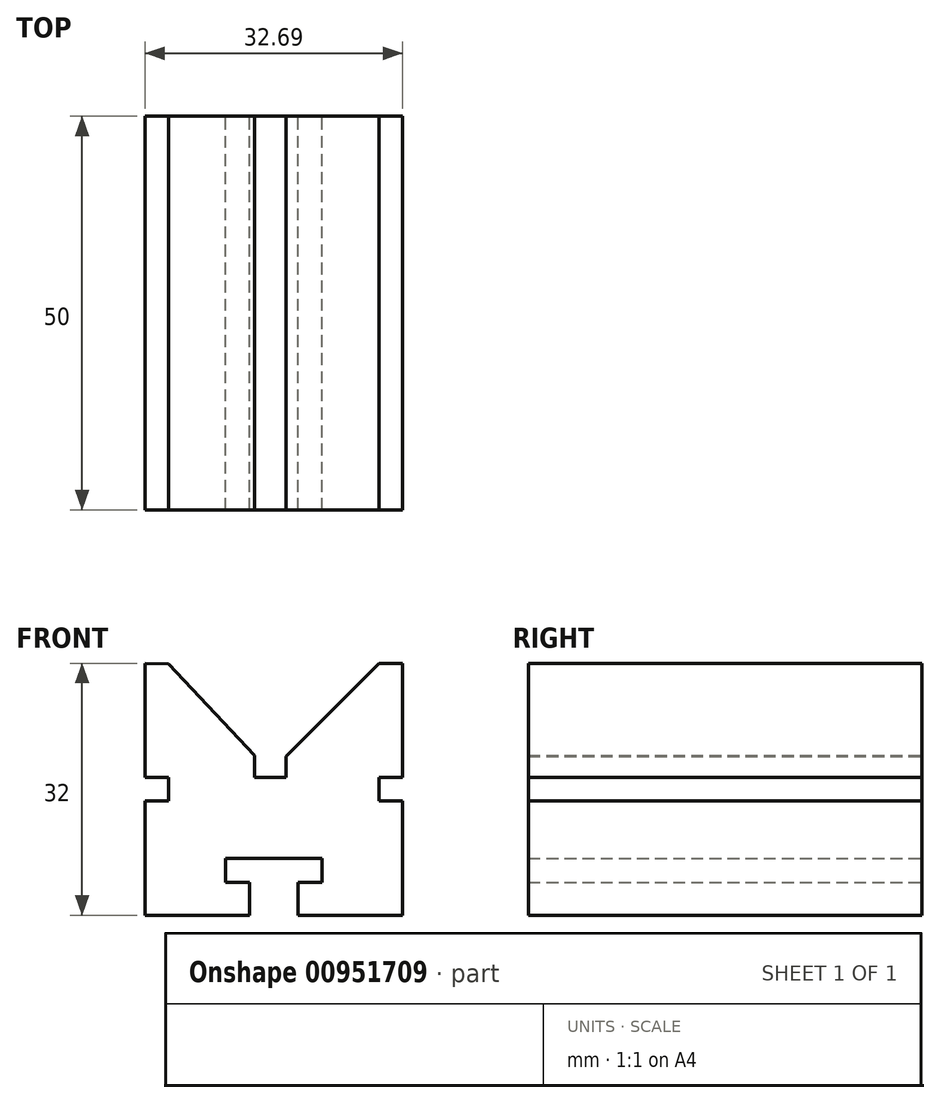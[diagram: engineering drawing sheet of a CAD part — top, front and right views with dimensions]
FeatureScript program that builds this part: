
annotation { "Feature Type Name" : "Feature", "Feature Type Description" : "" }
export const myFeature = defineFeature(function(context is Context, id is Id, definition is map)
    precondition{}
    {
        {
            var Q0;
            Q0=qCreatedBy(makeId("Front.planeOp"),FACE);
            var sketch = newSketch(context, id + "F0", { "sketchPlane" : qUnion([Q0])});
            skLineSegment(sketch, "E0.bottom", {"start": v(0, 0) * mm, "end": v(-13.24, 0) * mm});
            skLineSegment(sketch, "E0.left", {"start": v(0, 0) * mm, "end": v(0, 14.5) * mm});
            skLineSegment(sketch, "E0.right", {"start": v(-32.69, 0) * mm, "end": v(-32.69, 14.5) * mm});
            skLineSegment(sketch, "E1", {"start": v(-32.69, 32) * mm, "end": v(-29.69, 31.9) * mm});
            skLineSegment(sketch, "E2", {"start": v(-29.69, 31.9) * mm, "end": v(-18.8, 20.32) * mm});
            skPoint(sketch, "E2.endSnap0", {"position": v(-16.8, 32.44) * mm});
            skLineSegment(sketch, "E3", {"start": v(-14.8, 20.2) * mm, "end": v(-3, 32) * mm});
            skLineSegment(sketch, "E4", {"start": v(-3, 32) * mm, "end": v(0, 32) * mm});
            skLineSegment(sketch, "E5", {"start": v(0, 32) * mm, "end": v(0, 17.5) * mm});
            skLineSegment(sketch, "E6", {"start": v(0, 17.5) * mm, "end": v(-3, 17.5) * mm});
            skLineSegment(sketch, "E7", {"start": v(-3, 17.5) * mm, "end": v(-3, 14.5) * mm});
            skLineSegment(sketch, "E8", {"start": v(-3, 14.5) * mm, "end": v(0, 14.5) * mm});
            skLineSegment(sketch, "E9", {"start": v(-32.69, 17.5) * mm, "end": v(-29.69, 17.5) * mm});
            skLineSegment(sketch, "E10", {"start": v(-29.69, 17.5) * mm, "end": v(-29.69, 14.5) * mm});
            skLineSegment(sketch, "E11", {"start": v(-29.69, 14.5) * mm, "end": v(-32.69, 14.5) * mm});
            skLineSegment(sketch, "E12", {"start": v(-32.69, 0) * mm, "end": v(-19.44, 0) * mm});
            skLineSegment(sketch, "E13", {"start": v(-19.44, 0) * mm, "end": v(-19.44, 4.2) * mm});
            skLineSegment(sketch, "E14", {"start": v(-19.44, 4.2) * mm, "end": v(-22.44, 4.2) * mm});
            skLineSegment(sketch, "E15", {"start": v(-22.44, 4.2) * mm, "end": v(-22.44, 7.2) * mm});
            skLineSegment(sketch, "E16", {"start": v(-22.44, 7.2) * mm, "end": v(-10.24, 7.2) * mm});
            skLineSegment(sketch, "E17", {"start": v(-10.24, 7.2) * mm, "end": v(-10.24, 4.2) * mm});
            skLineSegment(sketch, "E18", {"start": v(-10.24, 4.2) * mm, "end": v(-13.24, 4.2) * mm});
            skLineSegment(sketch, "E19", {"start": v(-13.24, 4.2) * mm, "end": v(-13.24, 0) * mm});
            skLineSegment(sketch, "E20", {"start": v(-14.8, 17.5) * mm, "end": v(-16.8, 17.5) * mm});
            skLineSegment(sketch, "E21", {"start": v(-16.8, 17.5) * mm, "end": v(-18.8, 17.5) * mm});
            skLineSegment(sketch, "E22", {"start": v(-18.8, 17.5) * mm, "end": v(-18.8, 20.32) * mm});
            skLineSegment(sketch, "E23", {"start": v(-14.8, 17.5) * mm, "end": v(-14.8, 20.2) * mm});
            skPoint(sketch, "E24.orphan", {"position": v(-16.8, 18.2) * mm});
            skPoint(sketch, "E25.start.orphan", {"position": v(-32.69, 16) * mm});
            skLineSegment(sketch, "E26.trimOffspring", {"start": v(-32.69, 17.5) * mm, "end": v(-32.69, 32) * mm});
            skLineSegment(sketch, "E27.trimOffspring", {"start": v(-19.44, 0) * mm, "end": v(-32.69, 0) * mm});
            skPoint(sketch, "E28.orphan", {"position": v(-16.34, 0) * mm});
            skLineSegment(sketch, "E29.trimOffspring", {"start": v(0, 17.5) * mm, "end": v(0, 32) * mm});
            skPoint(sketch, "E30.orphan", {"position": v(0, 16) * mm});
            skSolve(sketch);
        }
        {
            var Q0;
            Q0=makeQuery(id+"F0.imprint","IMPRINT",FACE,{"disambiguationData":[TD([[makeQuery(id+"F0.imprint","IMPRINT",EDGE,{"derivedFrom":sQuery(id+"F0.wireOp",EDGE,"E0.bottom")}),-1.0]])]});
            extrude(context, id + "F1", {"entities" : qUnion([Q0]), "depth" : 50 * mm, "offsetDistance" : 25 * mm});
        }
    });
